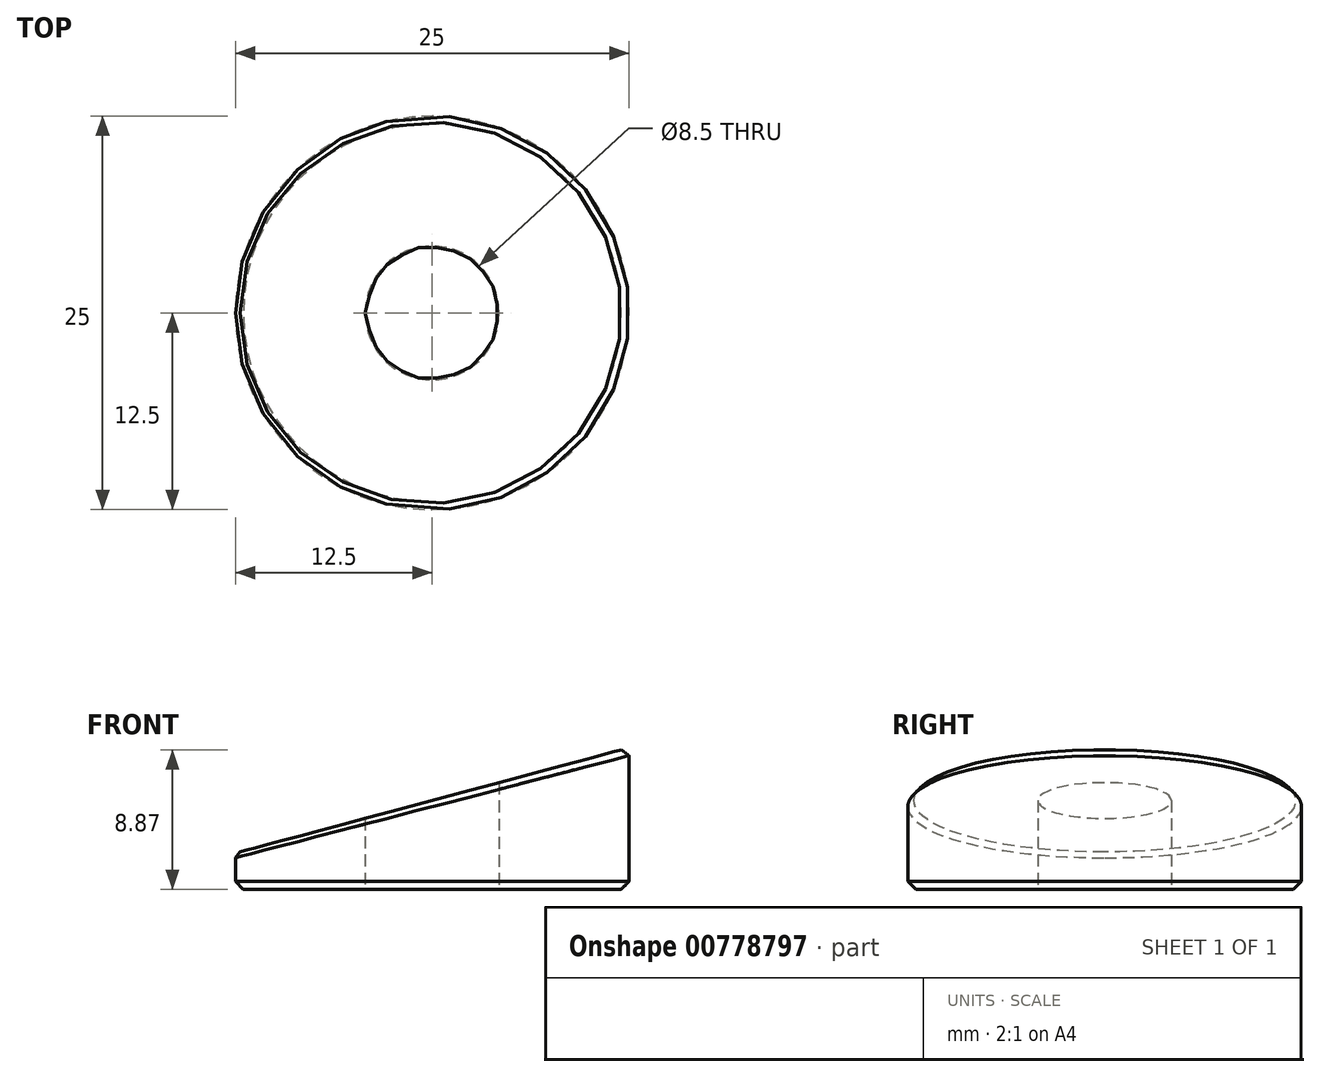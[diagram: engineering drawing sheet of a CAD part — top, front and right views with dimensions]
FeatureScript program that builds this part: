
annotation { "Feature Type Name" : "Feature", "Feature Type Description" : "" }
export const myFeature = defineFeature(function(context is Context, id is Id, definition is map)
    precondition{}
    {
        {
            var Q0;
            Q0=qCreatedBy(makeId("Top.planeOp"),FACE);
            var sketch = newSketch(context, id + "F0", { "sketchPlane" : qUnion([Q0])});
            skCircle(sketch, "E0", {"center": v(0, 0) * mm, "radius": 12.5 * mm});
            skCircle(sketch, "E1", {"center": v(0, 0) * mm, "radius": 4.25 * mm});
            skSolve(sketch);
        }
        {
            var Q0;
            Q0 = qSketchRegion(id + "F0", true);
            extrude(context, id + "F1", {"entities" : qUnion([Q0]), "depth" : 9 * mm, "offsetDistance" : 25 * mm});
        }
        {
            var Q0;
            Q0=qCreatedBy(makeId("Front.planeOp"),FACE);
            var sketch = newSketch(context, id + "F2", { "sketchPlane" : qUnion([Q0])});
            skLineSegment(sketch, "E2.0", {"start": v(-12.5, 9) * mm, "end": v(12.5, 9) * mm});
            skLineSegment(sketch, "E3", {"start": v(-12.5, 2.3) * mm, "end": v(-12.5, 10) * mm});
            skLineSegment(sketch, "E4", {"start": v(-12.5, 2.3) * mm, "end": v(12.5, 9) * mm});
            skSolve(sketch);
        }
        {
            var Q0;
            Q0 = qSketchRegion(id + "F2", true);
            extrude(context, id + "F3", {"entities" : qUnion([Q0]), "operationType" : NewBodyOperationType.REMOVE, "endBound" : BoundingType.THROUGH_ALL, "oppositeDirection" : true, "depth" : 25 * mm, "offsetDistance" : 25 * mm, "hasSecondDirection" : true, "secondDirectionBound" : BoundingType.THROUGH_ALL, "secondDirectionOppositeDirection" : false, "secondDirectionDepth" : 25 * mm});
        }
        {
            var Q0;
            Q0=makeQuery(id+"F3.boolean.opBoolean","INTERSECT",EDGE,{"derivedFrom":[makeQuery(id+"F1.opExtrude","SWEPT_FACE",FACE,{"disambiguationData":[OSD([sQuery(id+"F0.wireOp",EDGE,"E0")])]}),makeQuery(id+"F3.opExtrude","SWEPT_FACE",FACE,{"disambiguationData":[OSD([sQuery(id+"F2.wireOp",EDGE,"E4")])]})]});
            var Q1;
            Q1=makeQuery(id+"F1.opExtrude","CAP_EDGE",EDGE,{"disambiguationData":[OSD([sQuery(id+"F0.wireOp",EDGE,"E0")])],"isStart":true});
            chamfer(context, id + "F4", {"entities" : qUnion([Q0, Q1]), "width" : .5 * mm, "tangentPropagation" : true});
        }
    });
